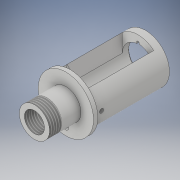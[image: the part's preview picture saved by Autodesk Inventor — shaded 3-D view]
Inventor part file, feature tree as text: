
AUTODESK INVENTOR PART (.ipt)
format: ipt  version: 2019 (Build 230136000, 136)  size: 365,568 bytes
history: native  units: mm
features: other x9, sketch x8, projected_geometry x7, extrude x6, chamfer x5, pattern_circular x2, hole x1
ambient origin geometry x8: Origin, YZ Plane, XZ Plane, XY Plane, X Axis, Y Axis, Z Axis, Center Point
bodies: Solide1 (feature_tree)
feature tree (38):
  other  "Révolution1"
  extrude  "Extrusion2"  Depth=38.0mm
  other  "Plan de construction1"
  hole  "Perçage1"  [1 undecoded]
  pattern_circular  "Réseau circulaire1"  [2 undecoded]
  other  "Filetage1"
  chamfer  "Chanfrein1"  Angle=165.0deg  [1 undecoded]
  extrude  "Extrusion3"  Depth=12.0mm
  chamfer  "Chanfrein2"  Distance=6.0mm
  chamfer  "Chanfrein4"  Distance=4.0mm
  chamfer  "Chanfrein5"  Distance=15.0mm
  chamfer  "Chanfrein6"  Distance=5.0mm
  other  "Plan de construction2"
  extrude  "Extrusion5"  Depth=16.0mm
  extrude  "Extrusion8"  TaperAngle=90.0deg  [1 undecoded]
  other  "Plan de construction8"
  extrude  "Extrusion9"  Depth=3.0mm
  pattern_circular  "Réseau circulaire2"  [2 undecoded]
  other  "Filetage2"
  other  "Plan de construction9"
  extrude  "Extrusion10"  Depth=10.0mm TaperAngle=0.0deg
  sketch  "Esquisse1"
  sketch  "Esquisse2"
  projected_geometry  "Boucle projetée1"
  projected_geometry  "Boucle projetée2"
  projected_geometry  "Boucle projetée3"
  sketch  "Esquisse3"
  sketch  "Esquisse4"
  projected_geometry  "Boucle projetée4"
  projected_geometry  "Boucle projetée5"
  projected_geometry  "Boucle projetée7"
  sketch  "Esquisse7"
  sketch  "Esquisse11"
  sketch  "Esquisse12"
  projected_geometry  "Boucle projetée8"
  sketch  "Esquisse13"
  other  "Projeter les arêtes coupées4"
  other  "Projeter les arêtes coupées5"
note: 7 required parameter values undecoded (feature->parameter linkage not recoverable at this tier; creation-order binding heuristic only, values carry confidence <= 0.55)
